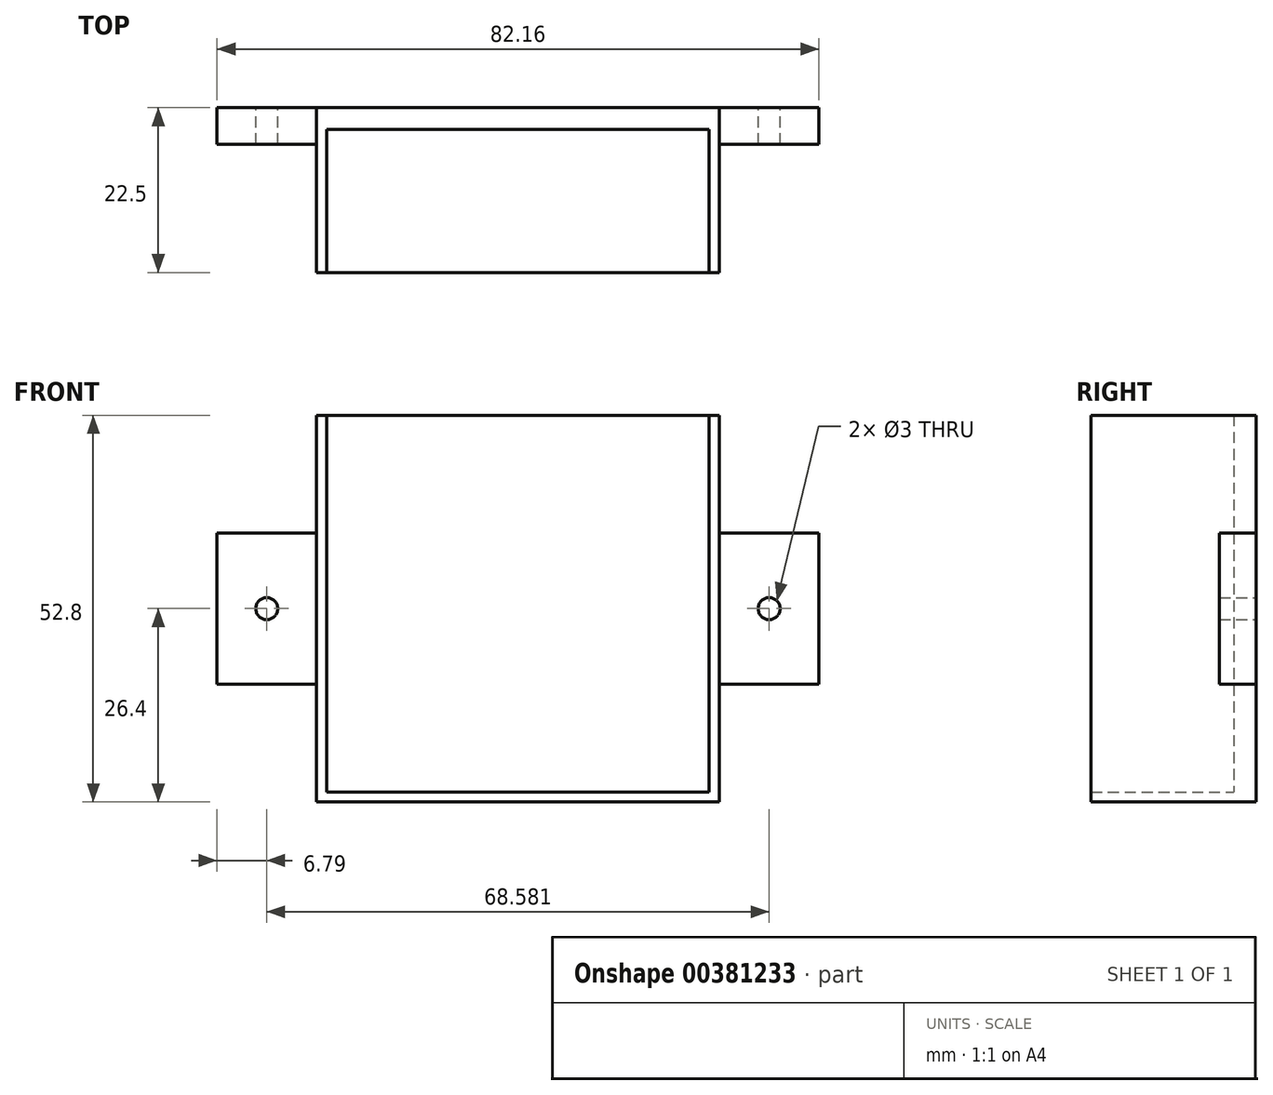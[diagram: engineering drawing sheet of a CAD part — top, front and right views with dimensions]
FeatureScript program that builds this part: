
annotation { "Feature Type Name" : "Feature", "Feature Type Description" : "" }
export const myFeature = defineFeature(function(context is Context, id is Id, definition is map)
    precondition{}
    {
        {
            var Q0;
            Q0=qCreatedBy(makeId("Front.planeOp"),FACE);
            var sketch = newSketch(context, id + "F0", { "sketchPlane" : qUnion([Q0])});
            skLineSegment(sketch, "E0.bottom", {"start": v(27.5, -26.4) * mm, "end": v(-27.5, -26.4) * mm});
            skLineSegment(sketch, "E0.top", {"start": v(27.5, 26.4) * mm, "end": v(-27.5, 26.4) * mm});
            skLineSegment(sketch, "E0.left", {"start": v(27.5, -26.4) * mm, "end": v(27.5, 26.4) * mm});
            skLineSegment(sketch, "E0.right", {"start": v(-27.5, -26.4) * mm, "end": v(-27.5, 26.4) * mm});
            skPoint(sketch, "E0.middle", {"position": v(0, 0) * mm});
            skPoint(sketch, "E1.right.start.orphan", {"position": v(-26.11, -24.94) * mm});
            skPoint(sketch, "E1.top.end.orphan", {"position": v(-26.09, 25.06) * mm});
            skPoint(sketch, "E1.left.end.orphan", {"position": v(26.11, 24.94) * mm});
            skPoint(sketch, "E1.left.start.orphan", {"position": v(26.09, -25.06) * mm});
            skLineSegment(sketch, "E2.top", {"start": v(-26.09, -25.06) * mm, "end": v(26.09, -25.06) * mm});
            skLineSegment(sketch, "E2.left", {"start": v(-26.09, 25.06) * mm, "end": v(-26.09, -25.06) * mm});
            skLineSegment(sketch, "E2.right", {"start": v(26.09, 25.06) * mm, "end": v(26.09, -25.06) * mm});
            skLineSegment(sketch, "E3", {"start": v(-26.09, 25.06) * mm, "end": v(-26.09, 26.4) * mm});
            skLineSegment(sketch, "E4", {"start": v(-26.09, 26.4) * mm, "end": v(-26.09, 30.2) * mm});
            skLineSegment(sketch, "E5", {"start": v(26.09, 25.06) * mm, "end": v(26.09, 30.2) * mm});
            skLineSegment(sketch, "E6", {"start": v(26.09, 30.2) * mm, "end": v(-26.09, 30.2) * mm});
            skLineSegment(sketch, "E7.bottom", {"start": v(41.08, -10.34) * mm, "end": v(27.5, -10.34) * mm});
            skLineSegment(sketch, "E7.top", {"start": v(41.08, 10.34) * mm, "end": v(27.5, 10.34) * mm});
            skLineSegment(sketch, "E7.left", {"start": v(41.08, -10.34) * mm, "end": v(41.08, 10.34) * mm});
            skLineSegment(sketch, "E7.right", {"start": v(-41.08, -10.34) * mm, "end": v(-41.08, 10.34) * mm});
            skPoint(sketch, "E8", {"position": v(-41.08, 0) * mm});
            skPoint(sketch, "E9", {"position": v(41.08, 0) * mm});
            skLineSegment(sketch, "E10", {"start": v(-27.5, 10.34) * mm, "end": v(-27.5, -10.34) * mm});
            skLineSegment(sketch, "E11", {"start": v(27.5, 10.34) * mm, "end": v(27.5, -10.34) * mm});
            skPoint(sketch, "E12", {"position": v(-27.5, 0) * mm});
            skPoint(sketch, "E13", {"position": v(-34.3, 0) * mm});
            skPoint(sketch, "E14", {"position": v(34.3, 0) * mm});
            skCircle(sketch, "E15", {"center": v(-34.3, 0) * mm, "radius": 1.5 * mm});
            skCircle(sketch, "E16", {"center": v(34.3, 0) * mm, "radius": 1.5 * mm});
            skLineSegment(sketch, "E17.trimOffspring", {"start": v(-27.5, -10.34) * mm, "end": v(-41.08, -10.34) * mm});
            skLineSegment(sketch, "E18.trimOffspring", {"start": v(-27.5, 10.34) * mm, "end": v(-41.08, 10.34) * mm});
            skPoint(sketch, "E19.orphan", {"position": v(27.5, 0) * mm});
            skSolve(sketch);
        }
        {
            var Q0;
            Q0=makeQuery(id+"F0.imprint","IMPRINT",FACE,{"disambiguationData":[TD([[makeQuery(id+"F0.imprint","IMPRINT",EDGE,{"derivedFrom":sQuery(id+"F0.wireOp",EDGE,"E2.top")}),1.0]])]});
            extrude(context, id + "F1", {"entities" : qUnion([Q0]), "depth" : 3 * mm});
        }
        {
            var Q0;
            {var subQ5=sQuery(id+"F0.wireOp",EDGE,"E0.bottom");Q0=makeQuery(id+"F0.imprint","IMPRINT",FACE,{"disambiguationData":[TD([[makeQuery(id+"F0.imprint","IMPRINT",EDGE,{"derivedFrom":subQ5}),-1.0]])]});}
            extrude(context, id + "F2", {"entities" : qUnion([Q0]), "operationType" : NewBodyOperationType.ADD, "depth" : 22.5 * mm});
        }
        {
            var Q0;
            Q0=makeQuery(id+"F0.imprint","IMPRINT",FACE,{"disambiguationData":[TD([[makeQuery(id+"F0.imprint","IMPRINT",EDGE,{"derivedFrom":sQuery(id+"F0.wireOp",EDGE,"E7.right")}),-1.0]])]});
            var Q1;
            Q1=makeQuery(id+"F0.imprint","IMPRINT",FACE,{"disambiguationData":[TD([[makeQuery(id+"F0.imprint","IMPRINT",EDGE,{"derivedFrom":sQuery(id+"F0.wireOp",EDGE,"E7.bottom")}),-1.0]])]});
            extrude(context, id + "F3", {"entities" : qUnion([Q0, Q1]), "operationType" : NewBodyOperationType.ADD, "depth" : 5 * mm});
        }
    });
